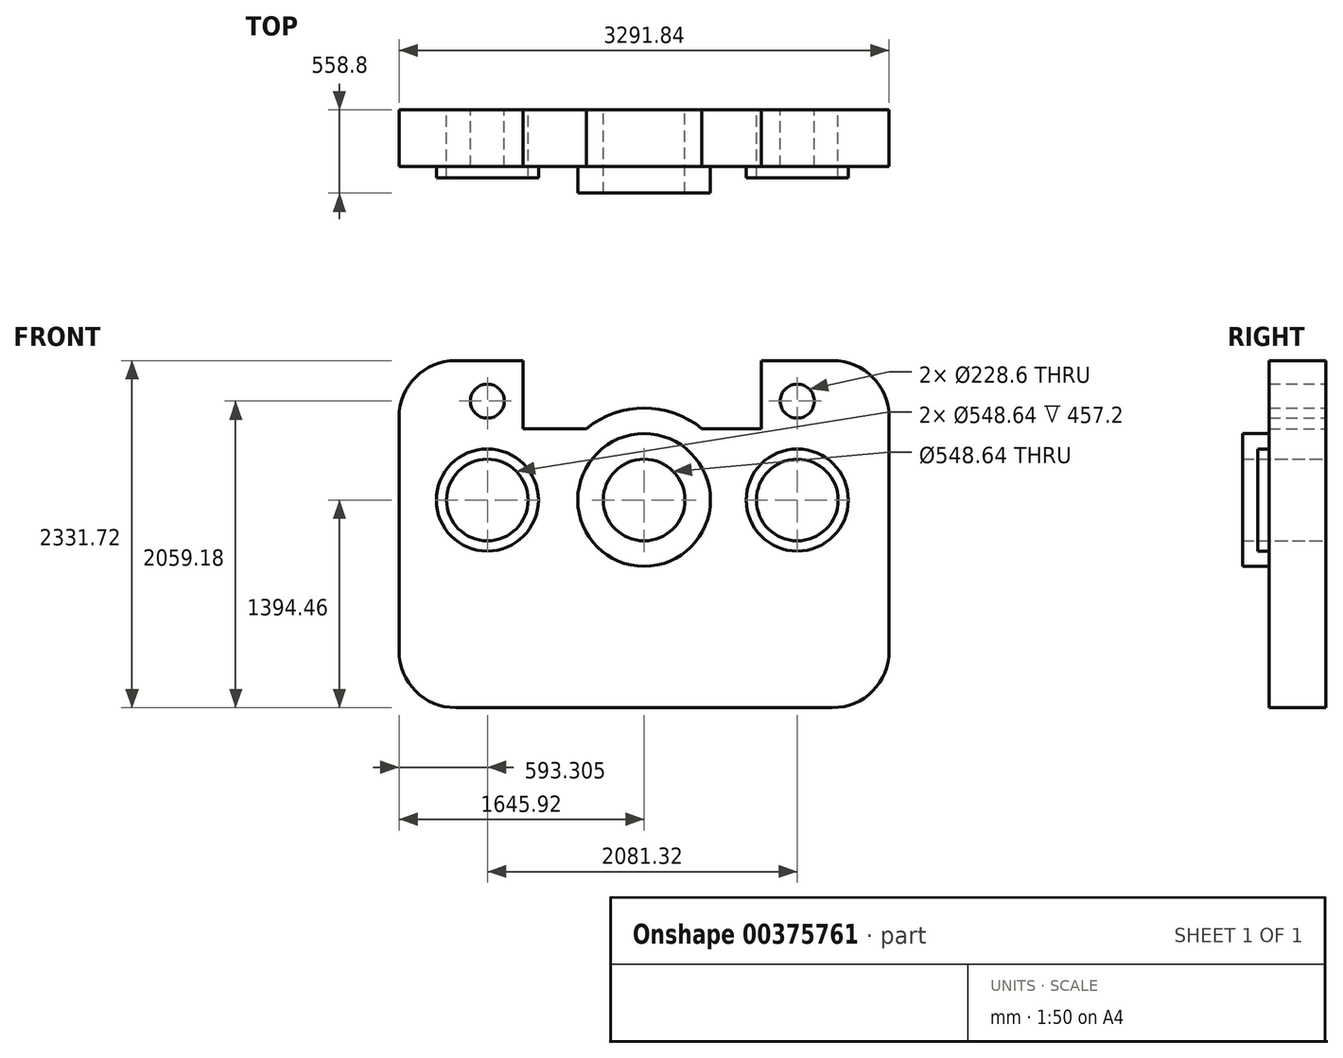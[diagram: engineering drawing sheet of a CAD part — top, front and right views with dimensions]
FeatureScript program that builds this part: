
annotation { "Feature Type Name" : "Feature", "Feature Type Description" : "" }
export const myFeature = defineFeature(function(context is Context, id is Id, definition is map)
    precondition{}
    {
        {
            var Q0;
            Q0=qCreatedBy(makeId("Front.planeOp"),FACE);
            var sketch = newSketch(context, id + "F0", { "sketchPlane" : qUnion([Q0])});
            skLineSegment(sketch, "E0", {"start": v(381, 0) * mm, "end": v(2910.84, 0) * mm});
            skLineSegment(sketch, "E1", {"start": v(3291.84, 381) * mm, "end": v(3291.84, 1950.72) * mm});
            skLineSegment(sketch, "E2", {"start": v(2910.84, 2331.72) * mm, "end": v(2434.6, 2331.72) * mm});
            skLineSegment(sketch, "E3", {"start": v(0, 1950.72) * mm, "end": v(0, 381) * mm});
            skPoint(sketch, "E4.visualSharp", {"position": v(0, 2331.72) * mm});
            skArc(sketch, "E4.filletArc", {"start": v(381, 2331.72) * mm, "mid": v(111.6, 2220.13) * mm, "end": v(0, 1950.72) * mm});
            skPoint(sketch, "E5.visualSharp", {"position": v(0, 0) * mm});
            skArc(sketch, "E5.filletArc", {"start": v(0, 381) * mm, "mid": v(111.6, 111.6) * mm, "end": v(381, 0) * mm});
            skPoint(sketch, "E6.visualSharp", {"position": v(3291.84, 0) * mm});
            skArc(sketch, "E6.filletArc", {"start": v(2910.84, 0) * mm, "mid": v(3180.25, 111.6) * mm, "end": v(3291.84, 381) * mm});
            skPoint(sketch, "E7.visualSharp", {"position": v(3291.84, 2331.72) * mm});
            skArc(sketch, "E7.filletArc", {"start": v(3291.84, 1950.72) * mm, "mid": v(3180.25, 2220.13) * mm, "end": v(2910.84, 2331.72) * mm});
            skLineSegment(sketch, "E8", {"start": v(833.33, 2331.72) * mm, "end": v(833.33, 1874.52) * mm});
            skLineSegment(sketch, "E9", {"start": v(833.33, 1874.52) * mm, "end": v(1257.97, 1874.52) * mm});
            skLineSegment(sketch, "E10", {"start": v(2434.6, 1874.52) * mm, "end": v(2434.6, 2331.72) * mm});
            skPoint(sketch, "E11.start.orphan", {"position": v(1645.92, 2331.72) * mm});
            skLineSegment(sketch, "E12.trimOffspring", {"start": v(833.33, 2331.72) * mm, "end": v(381, 2331.72) * mm});
            skArc(sketch, "E13", {"start": v(2033.87, 1874.52) * mm, "mid": v(1645.92, 2011.68) * mm, "end": v(1257.97, 1874.52) * mm});
            skLineSegment(sketch, "E14.trimOffspring", {"start": v(2033.87, 1874.52) * mm, "end": v(2434.6, 1874.52) * mm});
            skCircle(sketch, "E15", {"center": v(1645.92, 1394.46) * mm, "radius": 445.77 * mm});
            skCircle(sketch, "E16", {"center": v(1645.92, 1394.46) * mm, "radius": 274.32 * mm});
            skCircle(sketch, "E17", {"center": v(593.3, 1394.46) * mm, "radius": 342.9 * mm});
            skCircle(sketch, "E18", {"center": v(593.3, 1394.46) * mm, "radius": 274.32 * mm});
            skCircle(sketch, "E19", {"center": v(2674.62, 1394.46) * mm, "radius": 274.32 * mm});
            skCircle(sketch, "E20", {"center": v(2674.62, 1394.46) * mm, "radius": 342.9 * mm});
            skCircle(sketch, "E21", {"center": v(2674.62, 2059.18) * mm, "radius": 114.3 * mm});
            skCircle(sketch, "E22", {"center": v(593.3, 2059.18) * mm, "radius": 114.3 * mm});
            skSolve(sketch);
        }
        {
            var Q0;
            Q0=makeQuery(id+"F0.imprint","IMPRINT",FACE,{"disambiguationData":[TD([[makeQuery(id+"F0.imprint","IMPRINT",EDGE,{"derivedFrom":sQuery(id+"F0.wireOp",EDGE,"E0")}),1.0]])]});
            extrude(context, id + "F1", {"entities" : qUnion([Q0]), "depth" : 381 * mm});
        }
        {
            var Q0;
            Q0=makeQuery(id+"F0.imprint","IMPRINT",FACE,{"disambiguationData":[TD([[makeQuery(id+"F0.imprint","IMPRINT",EDGE,{"derivedFrom":sQuery(id+"F0.wireOp",EDGE,"E15")}),1.0]])]});
            extrude(context, id + "F2", {"entities" : qUnion([Q0]), "operationType" : NewBodyOperationType.ADD, "depth" : 558.8 * mm});
        }
        {
            var Q0;
            Q0=makeQuery(id+"F0.imprint","IMPRINT",FACE,{"disambiguationData":[TD([[makeQuery(id+"F0.imprint","IMPRINT",EDGE,{"derivedFrom":sQuery(id+"F0.wireOp",EDGE,"E17")}),1.0]])]});
            var Q1;
            Q1=makeQuery(id+"F0.imprint","IMPRINT",FACE,{"disambiguationData":[TD([[makeQuery(id+"F0.imprint","IMPRINT",EDGE,{"derivedFrom":sQuery(id+"F0.wireOp",EDGE,"E19")}),-1.0]])]});
            extrude(context, id + "F3", {"entities" : qUnion([Q0, Q1]), "operationType" : NewBodyOperationType.ADD, "depth" : 457.2 * mm});
        }
    });
